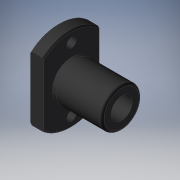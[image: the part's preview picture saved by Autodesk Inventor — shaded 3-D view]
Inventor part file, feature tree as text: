
AUTODESK INVENTOR PART (.ipt)
format: ipt  version: 2019 (Build 230136000, 136)  size: 170,496 bytes
history: native  units: mm
features: other x7, sketch x4, hole x2, revolve x1, extrude x1
ambient origin geometry x8: Origin, YZ Plane, XZ Plane, XY Plane, X Axis, Y Axis, Z Axis, Center Point
bodies: Solid1 (feature_tree)
feature tree (15):
  revolve  "Revolution1"  [1 undecoded]
  extrude  "Extrusion1"  TaperAngle=0.0deg  [1 undecoded]
  hole  "Hole1"  [1 undecoded]
  hole  "Hole2"  [1 undecoded]
  other  "Combination_Module_XY"
  other  "Combination_Module_YZ"
  other  "Combination_Module_ZX"
  other  "Combination_Module_X"
  other  "Combination_Module_Y"
  other  "Combination_Module_Z"
  other  "Combination_Module_Center"
  sketch  "Sketch_1"  dims[d0=360.0deg d1=5.0mm d2=0.0mm]
  sketch  "Sketch_3"  dims[d3=3.5mm d4=6.0mm d5=6.0mm d6=3.1mm d7=90.0deg d8=5.0mm d9=0.0mm]
  sketch  "Sketch3"  dims[d10=3.5mm d11=6.0mm d12=6.0mm d13=3.1mm d14=90.0deg d15=5.0mm d16=0.0mm d17=0.0mm]
  sketch  "Sketch4"
note: 4 required parameter values undecoded (feature->parameter linkage not recoverable at this tier; creation-order binding heuristic only, values carry confidence <= 0.55)